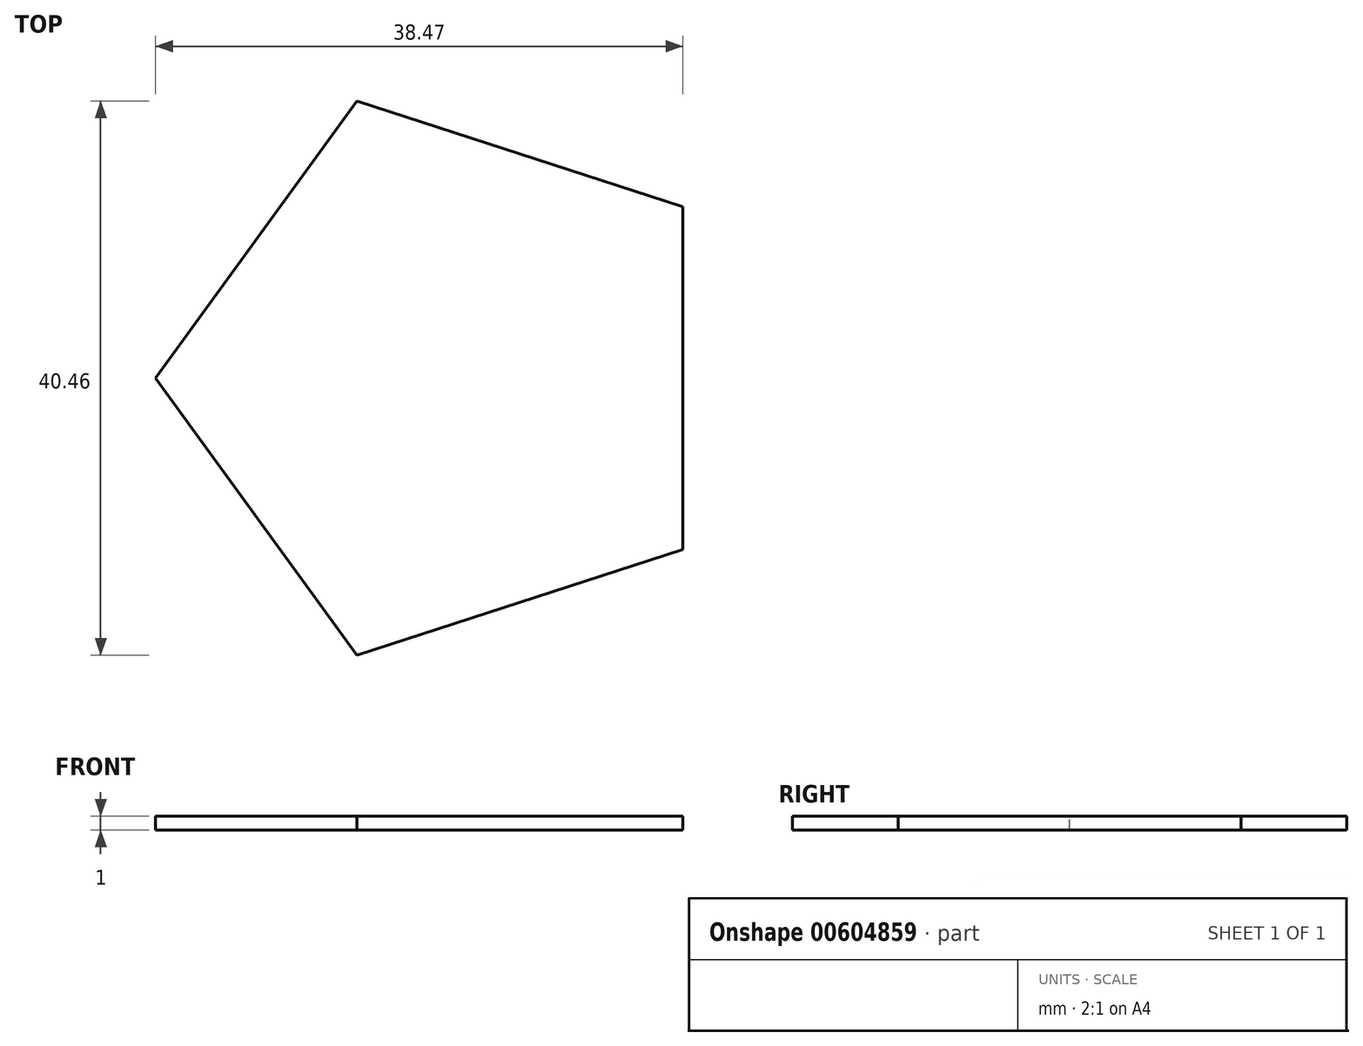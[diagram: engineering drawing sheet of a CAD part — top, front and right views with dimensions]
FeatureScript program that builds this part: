
annotation { "Feature Type Name" : "Feature", "Feature Type Description" : "" }
export const myFeature = defineFeature(function(context is Context, id is Id, definition is map)
    precondition{}
    {
        {
            var Q0;
            Q0=qCreatedBy(makeId("Top.planeOp"),FACE);
            var sketch = newSketch(context, id + "F0", { "sketchPlane" : qUnion([Q0])});
            skCircle(sketch, "E0.cCircle", {"center": v(0, 0) * mm, "radius": 21.27 * mm, "construction": true});
            skLineSegment(sketch, "E0.0", {"start": v(-21.27, 0) * mm, "end": v(-6.57, 20.23) * mm});
            skLineSegment(sketch, "E0.1", {"start": v(-6.57, 20.23) * mm, "end": v(17.2, 12.5) * mm});
            skLineSegment(sketch, "E0.2", {"start": v(17.2, 12.5) * mm, "end": v(17.2, -12.5) * mm});
            skLineSegment(sketch, "E0.3", {"start": v(17.2, -12.5) * mm, "end": v(-6.57, -20.23) * mm});
            skLineSegment(sketch, "E0.4", {"start": v(-6.57, -20.23) * mm, "end": v(-21.27, 0) * mm});
            skSolve(sketch);
        }
        {
            var Q0;
            Q0=makeQuery(id+"F0.imprint","IMPRINT",FACE,{"disambiguationData":[TD([[makeQuery(id+"F0.imprint","IMPRINT",EDGE,{"derivedFrom":sQuery(id+"F0.wireOp",EDGE,"E0.0")}),-1.0]])]});
            extrude(context, id + "F1", {"entities" : qUnion([Q0]), "oppositeDirection" : true, "depth" : 1 * mm, "offsetDistance" : 25.4 * mm});
        }
    });
